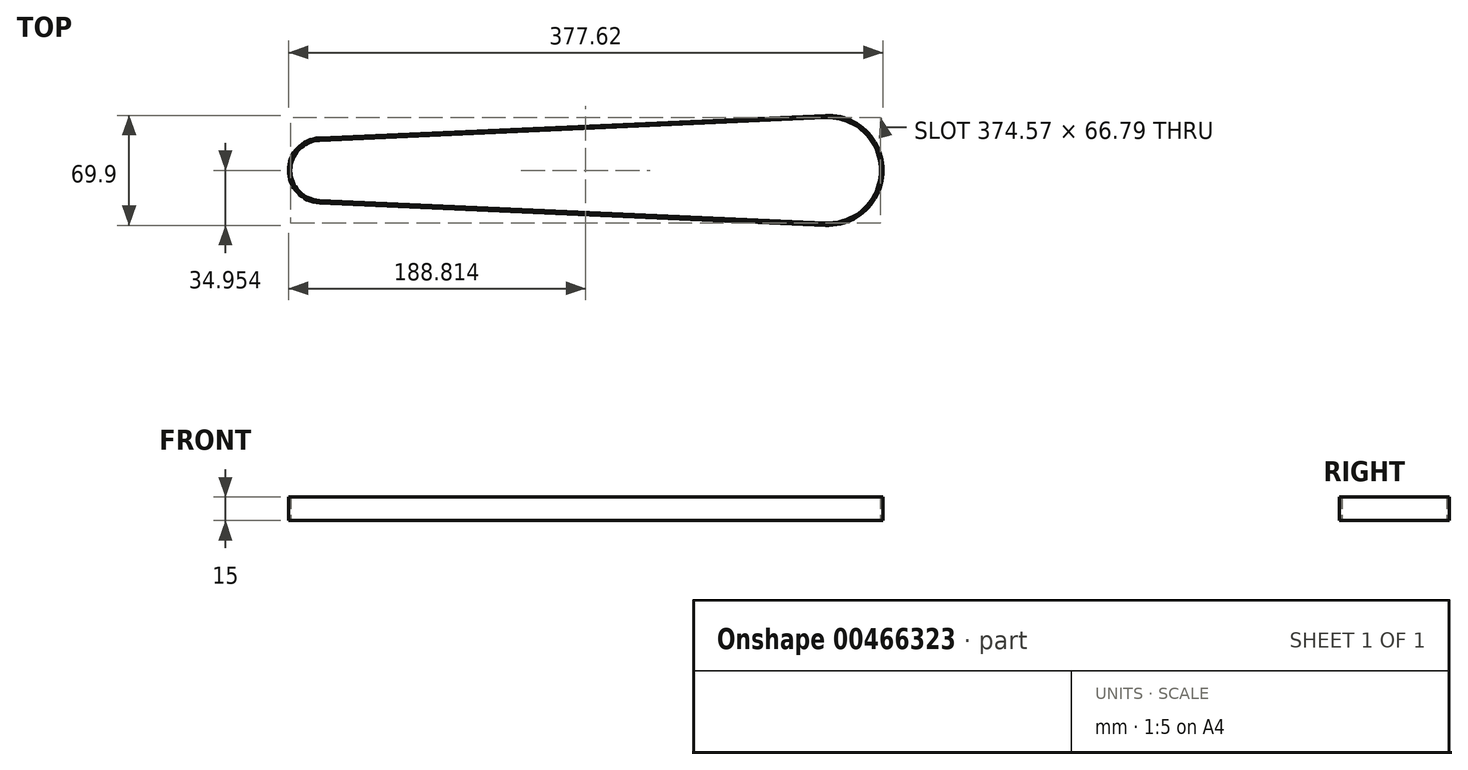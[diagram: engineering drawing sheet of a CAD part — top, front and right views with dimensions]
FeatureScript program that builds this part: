
annotation { "Feature Type Name" : "Feature", "Feature Type Description" : "" }
export const myFeature = defineFeature(function(context is Context, id is Id, definition is map)
    precondition{}
    {
        {
            var Q0;
            Q0=qCreatedBy(makeId("Top.planeOp"),FACE);
            var sketch = newSketch(context, id + "F0", { "sketchPlane" : qUnion([Q0])});
            skLineSegment(sketch, "E0", {"start": v(-154.13, -161) * mm, "end": v(167.28, -146.68) * mm});
            skLineSegment(sketch, "E1", {"start": v(-154.13, -199.16) * mm, "end": v(167.28, -213.47) * mm});
            skArc(sketch, "E2", {"start": v(-154.2, -159.47) * mm, "mid": v(-173.9, -180.08) * mm, "end": v(-154.2, -200.68) * mm});
            skArc(sketch, "E3", {"start": v(167.2, -215) * mm, "mid": v(203.71, -180.08) * mm, "end": v(167.2, -145.16) * mm});
            skLineSegment(sketch, "E4", {"start": v(167.2, -145.16) * mm, "end": v(-154.2, -159.47) * mm});
            skLineSegment(sketch, "E5", {"start": v(-154.2, -200.68) * mm, "end": v(167.2, -215) * mm});
            skArc(sketch, "E6", {"start": v(-154.13, -161) * mm, "mid": v(-172.38, -180.08) * mm, "end": v(-154.13, -199.16) * mm});
            skArc(sketch, "E7", {"start": v(167.28, -213.47) * mm, "mid": v(202.2, -180.08) * mm, "end": v(167.28, -146.68) * mm});
            skLineSegment(sketch, "E8", {"start": v(-153.28, -180.08) * mm, "end": v(168.76, -180.08) * mm});
            skLineSegment(sketch, "E9", {"start": v(168.76, -180.08) * mm, "end": v(168.76, -180.08) * mm});
            skSolve(sketch);
        }
        {
            var Q0;
            {var subQ1=sQuery(id+"F0.wireOp",EDGE,"E0");Q0=makeQuery(id+"F0.imprint","IMPRINT",FACE,{"disambiguationData":[TD([[makeQuery(id+"F0.imprint","IMPRINT",EDGE,{"derivedFrom":subQ1}),1.0]])]});}
            extrude(context, id + "F1", {"entities" : qUnion([Q0]), "depth" : 15 * mm});
        }
    });
